# Revit family: Profile-Slab Edge-Steel & Tube-ComFlor-Edge Trim
name_source: partatom
category: Profiles
revit_build: Autodesk Revit 2016 (Build: 20160314_0715(x64)
units: mm (PartAtom-declared; Revit-internal decimal feet)

## family parameters
Material for Model Behavior = Other
Profile Usage = Slab Edge
Rotate with component = No

## types (5) — shared parameters
CBICode = 3151
CBIDescription = Composite construction of in situ concrete and permanent formwork
ComFlor Design Software = http://www.comflor.co.nz
ComFlor Technical Resources = http://www.comflor.co.nz
Description = Edge trim for use with ComFlor® range.
Leg Length = 50 mm  [stored 0.164042 ft]
Manufacturer = ComFlor
ManufacturerName = ComFlor
ManufacturerURL = http://www.steelandtube.co.nz
ModifiedIssue_ANZRS = 20160719.01 $
Slab Depth = 270 mm  [stored 0.885827 ft]
SpecificationDescription = ComFlor composite floor system
SpecificationReference = 3151C
Tata Steel UK Limited = ComFlor® is a registered trade mark used in Australia and New Zealand under licence from Tata Steel UK Limited.
Type Comments = Refer span tables for maximum cantilever
URL = http://www.comflor.co.nz
Uniclass2015Code = Ss_30_12_85_16
Uniclass2015Title = Composite steel and concrete floor, roof or balcony deck systems
Uniclass2015Version = 2015

## per-type parameters (varying)
| type | BMT |
| BMT-0.9mm | 1 mm  [stored 0.00328084 ft] |
| BMT-1.0mm | 1 mm  [stored 0.00328084 ft] |
| BMT-1.2mm | 1 mm  [stored 0.00328084 ft] |
| BMT-1.6mm | 2 mm  [stored 0.00656168 ft] |
| BMT-2.0mm | 2 mm  [stored 0.00656168 ft] |

note: [stored X ft] marks values corroborated as IEEE doubles in the binary element streams (Revit-internal decimal feet)

## geometry (parser evidence)
native form markers: Sweep x1
no freeform markers — native parametric forms only
